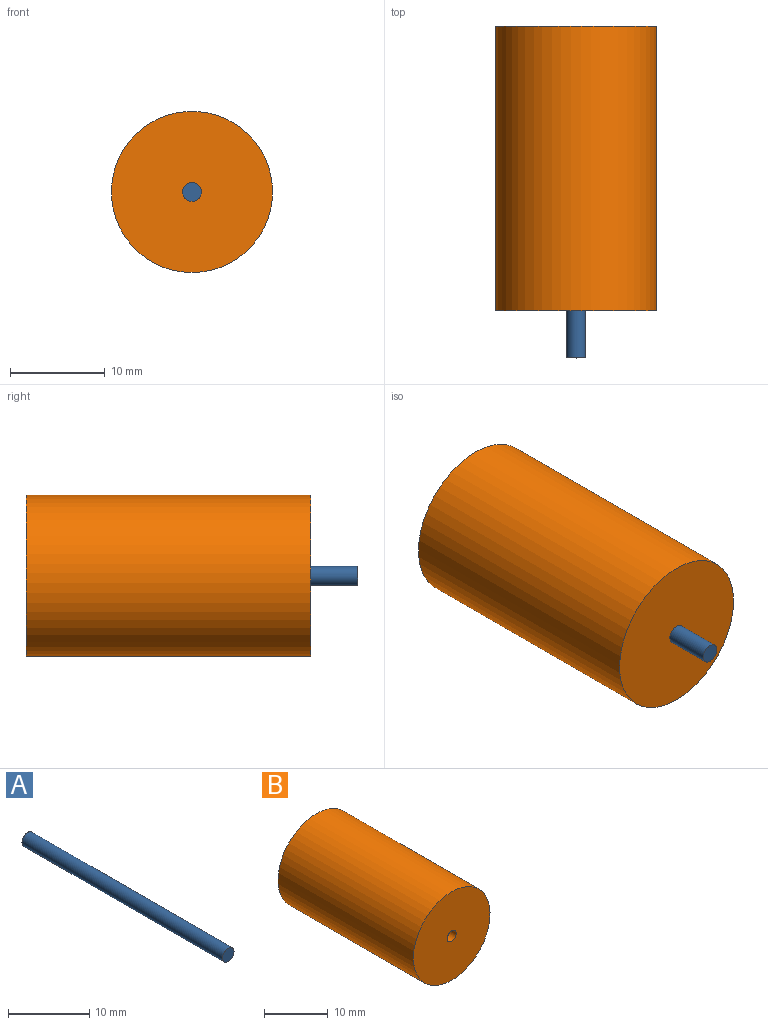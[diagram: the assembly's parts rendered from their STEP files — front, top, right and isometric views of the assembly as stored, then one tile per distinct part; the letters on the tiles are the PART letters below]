
ASSEMBLY  parts=2 mates=1
PART A: 3 faces, bbox 2x35x2 mm
  f0: cylinder r=1mm len=35mm, axis (0,1,0), area 219.9mm2, adj f1,f2
  f1: plane 2x2mm, normal (0,-1,0), area 3.1mm2, adj f0
  f2: plane 2x2mm, normal (0,1,0), area 3.1mm2, adj f0
PART B: 4 faces, bbox 17x30x17 mm
  f0: cylinder r=1mm len=30mm, axis (0,1,0), area 188.5mm2, adj f2,f3
  f1: cylinder r=8.5mm len=30mm, axis (0,1,0), area 1602.2mm2, adj f2,f3
  f2: plane 17x17mm, normal (0,-1,0), area 223.8mm2, adj f0,f1
  f3: plane 17x17mm, normal (0,1,0), area 223.8mm2, adj f0,f1
PLACE A at identity
PLACE B at identity
MATE revolute A.f0 <-> B.f0  axis (0,1,0) through (0,0,0)mm
